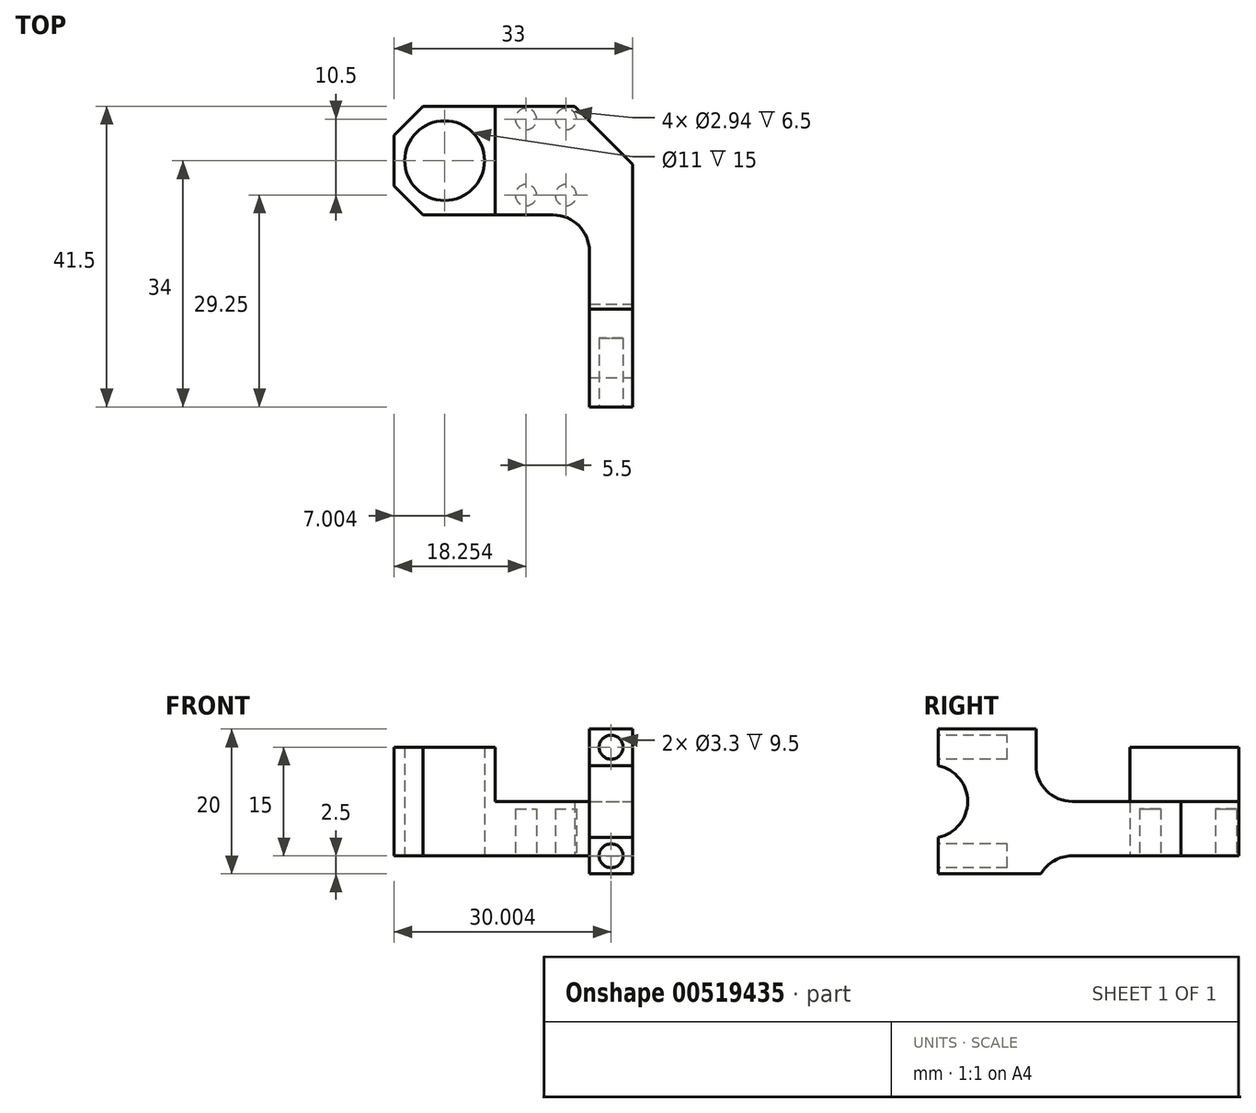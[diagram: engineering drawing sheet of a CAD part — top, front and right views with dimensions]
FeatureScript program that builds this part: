
annotation { "Feature Type Name" : "Feature", "Feature Type Description" : "" }
export const myFeature = defineFeature(function(context is Context, id is Id, definition is map)
    precondition{}
    {
        {
            var Q0;
            Q0=qCreatedBy(makeId("Top.planeOp"),FACE);
            var sketch = newSketch(context, id + "F0", { "sketchPlane" : qUnion([Q0])});
            skLineSegment(sketch, "E0", {"start": v(22.32, 7) * mm, "end": v(22.32, -26.5) * mm});
            skLineSegment(sketch, "E1", {"start": v(16.32, -26.5) * mm, "end": v(16.32, 0) * mm});
            skLineSegment(sketch, "E2", {"start": v(16.32, 0) * mm, "end": v(-6.68, 0) * mm});
            skLineSegment(sketch, "E3", {"start": v(-6.68, 0) * mm, "end": v(-10.68, 4) * mm});
            skLineSegment(sketch, "E4", {"start": v(-10.68, 4) * mm, "end": v(-10.68, 11) * mm});
            skLineSegment(sketch, "E5", {"start": v(-10.68, 11) * mm, "end": v(-6.68, 15) * mm});
            skLineSegment(sketch, "E6", {"start": v(-6.68, 15) * mm, "end": v(14.32, 15) * mm});
            skLineSegment(sketch, "E7", {"start": v(22.32, 7) * mm, "end": v(14.32, 15) * mm});
            skLineSegment(sketch, "E8", {"start": v(16.32, -26.5) * mm, "end": v(22.32, -26.5) * mm});
            skCircle(sketch, "E9", {"center": v(-3.68, 7.5) * mm, "radius": 5.5 * mm});
            skSolve(sketch);
        }
        {
            var Q0;
            Q0 = qSketchRegion(id + "F0", true);
            extrude(context, id + "F1", {"entities" : qUnion([Q0]), "depth" : 20 * mm, "offsetDistance" : 25 * mm});
        }
        {
            var Q0;
            Q0=makeQuery(id+"F1.opExtrude","SWEPT_EDGE",EDGE,{"disambiguationData":[OSD([sQuery(id+"F0.wireOp",EDGE,"E1"),sQuery(id+"F0.wireOp",EDGE,"E2")])]});
            fillet(context, id + "F2", {"entities" : qUnion([Q0]), "radius" : 5 * mm, "tangentPropagation" : true, "allowEdgeOverflow" : false});
        }
        {
            var Q0;
            Q0=makeQuery(id+"F1.opExtrude","SWEPT_FACE",FACE,{"disambiguationData":[OSD([sQuery(id+"F0.wireOp",EDGE,"E0")])]});
            var sketch = newSketch(context, id + "F3", { "sketchPlane" : qUnion([Q0])});
            skLineSegment(sketch, "E10.bottom", {"start": v(-13, 20) * mm, "end": v(15, 20) * mm});
            skLineSegment(sketch, "E10.top", {"start": v(-13, 10) * mm, "end": v(15, 10) * mm});
            skLineSegment(sketch, "E10.left", {"start": v(-13, 20) * mm, "end": v(-13, 10) * mm});
            skLineSegment(sketch, "E10.right", {"start": v(15, 20) * mm, "end": v(15, 10) * mm});
            skSolve(sketch);
        }
        {
            var Q0;
            Q0 = qSketchRegion(id + "F3", true);
            extrude(context, id + "F4", {"entities" : qUnion([Q0]), "operationType" : NewBodyOperationType.REMOVE, "oppositeDirection" : true, "depth" : 19 * mm, "offsetDistance" : 25 * mm});
        }
        {
            var Q0;
            {var subQ0=sQuery(id+"F0.wireOp",EDGE,"E5");var subQ1=sQuery(id+"F0.wireOp",EDGE,"E4");var subQ2=sQuery(id+"F0.wireOp",EDGE,"E3");var subQ3=sQuery(id+"F0.wireOp",EDGE,"E2");var subQ4=sQuery(id+"F0.wireOp",EDGE,"E6");var subQ5=sQuery(id+"F0.wireOp",EDGE,"E9");Q0=makeQuery(id+"F4.boolean.opBoolean","SPLIT",FACE,{"disambiguationData":[TD([makeQuery(id+"F1.opExtrude","SWEPT_FACE",FACE,{"disambiguationData":[OSD([subQ3])]})])],"derivedFrom":makeQuery(id+"F1.opExtrude","CAP_FACE",FACE,{"disambiguationData":[OSD([sQuery(id+"F0.wireOp",EDGE,"E0"),sQuery(id+"F0.wireOp",EDGE,"E1"),subQ3,subQ2,subQ1,subQ0,subQ4,sQuery(id+"F0.wireOp",EDGE,"E7"),sQuery(id+"F0.wireOp",EDGE,"E8"),subQ5])],"isStart":false})});}
            var sketch = newSketch(context, id + "F5", { "sketchPlane" : qUnion([Q0])});
            skLineSegment(sketch, "E11.bottom", {"start": v(3.32, 15) * mm, "end": v(-10.68, 15) * mm});
            skLineSegment(sketch, "E11.top", {"start": v(3.32, 0) * mm, "end": v(-10.68, 0) * mm});
            skLineSegment(sketch, "E11.left", {"start": v(3.32, 15) * mm, "end": v(3.32, 0) * mm});
            skLineSegment(sketch, "E11.right", {"start": v(-10.68, 15) * mm, "end": v(-10.68, 0) * mm});
            skSolve(sketch);
        }
        {
            var Q0;
            Q0 = qSketchRegion(id + "F5", true);
            extrude(context, id + "F6", {"entities" : qUnion([Q0]), "operationType" : NewBodyOperationType.REMOVE, "oppositeDirection" : true, "depth" : 2.5 * mm, "offsetDistance" : 25 * mm});
        }
        {
            var Q0;
            Q0=makeQuery(id+"F4.boolean.opBoolean","COPY",EDGE,{"derivedFrom":makeQuery(id+"F4.opExtrude","SWEPT_EDGE",EDGE,{"disambiguationData":[OSD([sQuery(id+"F3.wireOp",EDGE,"E10.top"),sQuery(id+"F3.wireOp",EDGE,"E10.left")])]})});
            fillet(context, id + "F7", {"entities" : qUnion([Q0]), "radius" : 5 * mm, "tangentPropagation" : true, "allowEdgeOverflow" : false});
        }
        {
            var Q0;
            Q0=makeQuery(id+"F1.opExtrude","SWEPT_FACE",FACE,{"disambiguationData":[OSD([sQuery(id+"F0.wireOp",EDGE,"E0")])]});
            var sketch = newSketch(context, id + "F8", { "sketchPlane" : qUnion([Q0])});
            skPoint(sketch, "E12.firstSnap0", {"position": v(-9.75, 0) * mm});
            skLineSegment(sketch, "E12.bottom", {"start": v(-13, -12.28) * mm, "end": v(27.7, -12.28) * mm});
            skLineSegment(sketch, "E12.top", {"start": v(-8, 2.5) * mm, "end": v(27.7, 2.5) * mm});
            skLineSegment(sketch, "E12.left", {"start": v(-13, -12.28) * mm, "end": v(-13, -2.5) * mm});
            skLineSegment(sketch, "E12.right", {"start": v(27.7, -12.28) * mm, "end": v(27.7, 2.5) * mm});
            skPoint(sketch, "E13.visualSharp", {"position": v(-13, 2.5) * mm});
            skArc(sketch, "E13.filletArc", {"start": v(-8, 2.5) * mm, "mid": v(-11.54, 1.04) * mm, "end": v(-13, -2.5) * mm});
            skCircle(sketch, "E14", {"center": v(-27.5, 10) * mm, "radius": 5.05 * mm});
            skSolve(sketch);
        }
        {
            var Q0;
            Q0 = qSketchRegion(id + "F8", true);
            extrude(context, id + "F9", {"entities" : qUnion([Q0]), "operationType" : NewBodyOperationType.REMOVE, "oppositeDirection" : true, "depth" : 33 * mm, "offsetDistance" : 25 * mm});
        }
        {
            var Q0;
            {var subQ0=sQuery(id+"F0.wireOp",EDGE,"E0");var subQ1=sQuery(id+"F0.wireOp",EDGE,"E8");var subQ2=sQuery(id+"F0.wireOp",EDGE,"E1");Q0=makeQuery(id+"F9.boolean.opBoolean","SPLIT",FACE,{"disambiguationData":[TD([makeQuery(id+"F1.opExtrude","CAP_FACE",FACE,{"disambiguationData":[OSD([subQ0,subQ2,sQuery(id+"F0.wireOp",EDGE,"E2"),sQuery(id+"F0.wireOp",EDGE,"E3"),sQuery(id+"F0.wireOp",EDGE,"E4"),sQuery(id+"F0.wireOp",EDGE,"E5"),sQuery(id+"F0.wireOp",EDGE,"E6"),sQuery(id+"F0.wireOp",EDGE,"E7"),subQ1,sQuery(id+"F0.wireOp",EDGE,"E9")])],"isStart":false})])],"derivedFrom":makeQuery(id+"F1.opExtrude","SWEPT_FACE",FACE,{"disambiguationData":[OSD([subQ1])]})});}
            var sketch = newSketch(context, id + "F10", { "sketchPlane" : qUnion([Q0])});
            skCircle(sketch, "E15", {"center": v(19.32, 17.5) * mm, "radius": 1.65 * mm});
            skCircle(sketch, "E16", {"center": v(19.32, 2.5) * mm, "radius": 1.65 * mm});
            skPoint(sketch, "E16.centerSnap0", {"position": v(19.32, 14.95) * mm});
            skSolve(sketch);
        }
        {
            var Q0;
            Q0 = qSketchRegion(id + "F10", true);
            extrude(context, id + "F11", {"entities" : qUnion([Q0]), "operationType" : NewBodyOperationType.REMOVE, "oppositeDirection" : true, "depth" : 9.5 * mm, "offsetDistance" : 25 * mm});
        }
        {
            var Q0;
            Q0=makeQuery(id+"F9.boolean.opBoolean","COPY",FACE,{"derivedFrom":makeQuery(id+"F9.opExtrude","SWEPT_FACE",FACE,{"disambiguationData":[OSD([sQuery(id+"F8.wireOp",EDGE,"E12.top")])]})});
            var sketch = newSketch(context, id + "F12", { "sketchPlane" : qUnion([Q0])});
            skCircle(sketch, "E17", {"center": v(7.57, -2.75) * mm, "radius": 1.47 * mm});
            skCircle(sketch, "E18.0.1.0", {"center": v(7.57, -13.25) * mm, "radius": 1.47 * mm});
            skCircle(sketch, "E18.1.0.0", {"center": v(13.07, -2.75) * mm, "radius": 1.47 * mm});
            skCircle(sketch, "E18.1.1.0", {"center": v(13.07, -13.25) * mm, "radius": 1.47 * mm});
            skLineSegment(sketch, "E18.direction1", {"start": v(7.57, -2.75) * mm, "end": v(13.07, -2.75) * mm, "construction": true});
            skLineSegment(sketch, "E18.direction2", {"start": v(7.57, -2.75) * mm, "end": v(7.57, -13.25) * mm, "construction": true});
            skSolve(sketch);
        }
        {
            var Q0;
            Q0 = qSketchRegion(id + "F12", true);
            extrude(context, id + "F13", {"entities" : qUnion([Q0]), "operationType" : NewBodyOperationType.REMOVE, "oppositeDirection" : true, "depth" : 6.5 * mm, "offsetDistance" : 25 * mm});
        }
    });
